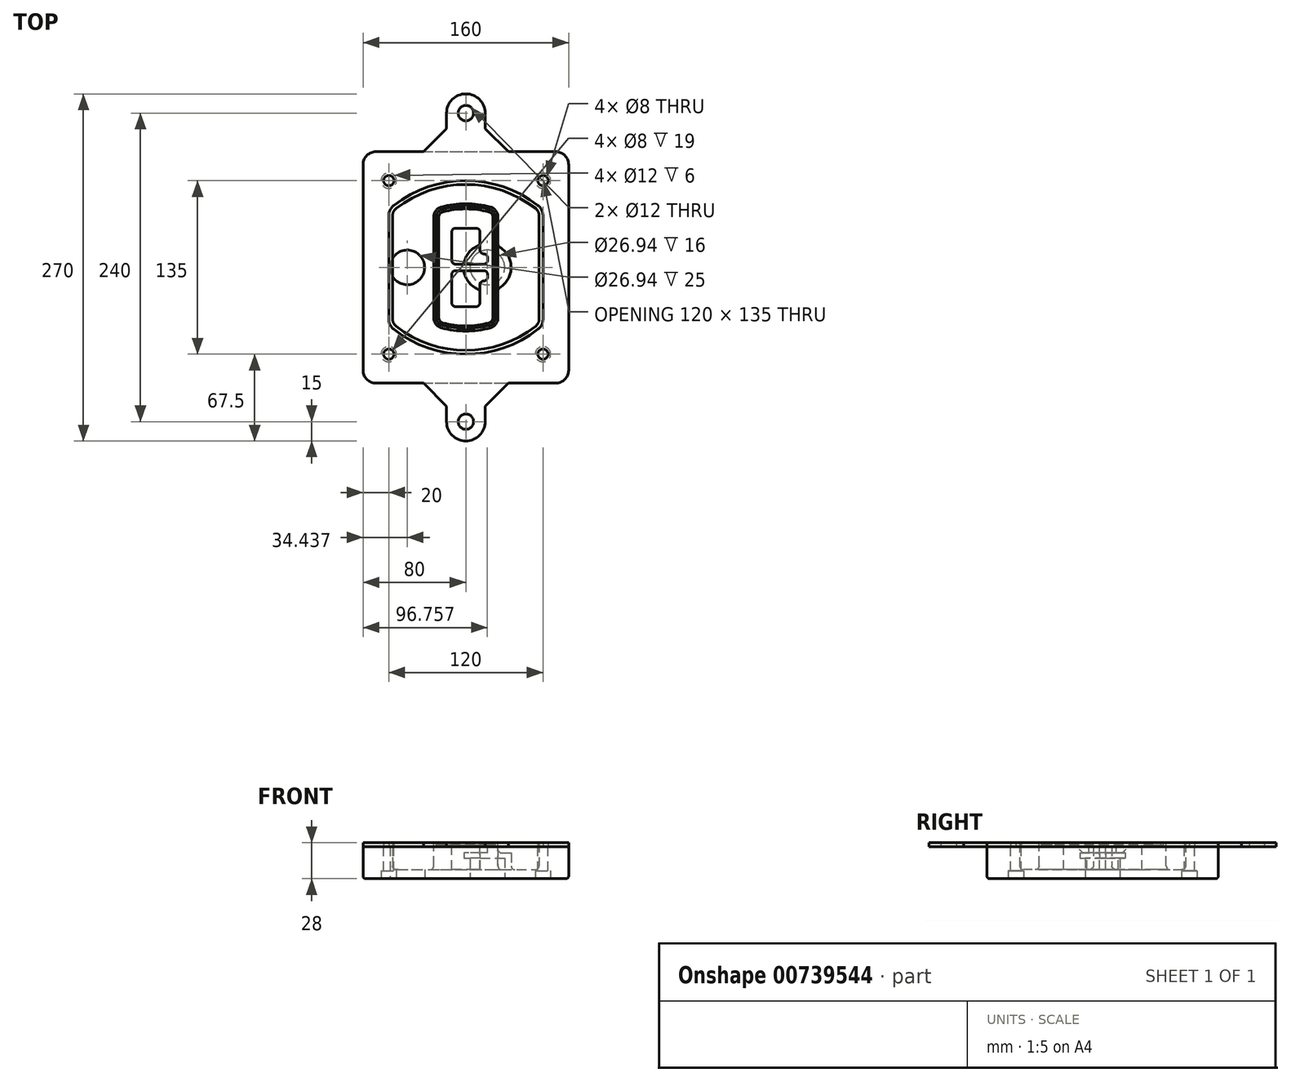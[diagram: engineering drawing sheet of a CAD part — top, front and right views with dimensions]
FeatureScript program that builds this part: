
annotation { "Feature Type Name" : "Feature", "Feature Type Description" : "" }
export const myFeature = defineFeature(function(context is Context, id is Id, definition is map)
    precondition{}
    {
        {
            var Q0;
            Q0=qCreatedBy(makeId("Top.planeOp"),FACE);
            var sketch = newSketch(context, id + "F0", { "sketchPlane" : qUnion([Q0])});
            skPoint(sketch, "E0.rect.middle", {"position": v(0, 0) * mm});
            skLineSegment(sketch, "E1.bottom", {"start": v(-70, -90) * mm, "end": v(70, -90) * mm});
            skLineSegment(sketch, "E1.top", {"start": v(-70, 90) * mm, "end": v(70, 90) * mm});
            skLineSegment(sketch, "E1.left", {"start": v(-80, -80) * mm, "end": v(-80, 80) * mm});
            skLineSegment(sketch, "E1.right", {"start": v(80, -80) * mm, "end": v(80, 80) * mm});
            skLineSegment(sketch, "E2", {"start": v(-80, 90) * mm, "end": v(80, -90) * mm, "construction": true});
            skLineSegment(sketch, "E3", {"start": v(80, 90) * mm, "end": v(-80, -90) * mm, "construction": true});
            skCircle(sketch, "E4", {"center": v(-60, 67.5) * mm, "radius": 4 * mm});
            skCircle(sketch, "E5", {"center": v(60, 67.5) * mm, "radius": 4 * mm});
            skCircle(sketch, "E6", {"center": v(60, -67.5) * mm, "radius": 4 * mm});
            skCircle(sketch, "E7", {"center": v(-60, -67.5) * mm, "radius": 4 * mm});
            skLineSegment(sketch, "E8", {"start": v(-60, 67.5) * mm, "end": v(60, 67.5) * mm, "construction": true});
            skLineSegment(sketch, "E9", {"start": v(60, 67.5) * mm, "end": v(60, -67.5) * mm, "construction": true});
            skLineSegment(sketch, "E10", {"start": v(60, -67.5) * mm, "end": v(-60, -67.5) * mm, "construction": true});
            skLineSegment(sketch, "E11", {"start": v(-60, -67.5) * mm, "end": v(-60, 67.5) * mm, "construction": true});
            skLineSegment(sketch, "E12", {"start": v(-60, 40.3) * mm, "end": v(-60, -40.3) * mm});
            skLineSegment(sketch, "E13", {"start": v(60, 40.3) * mm, "end": v(60, -40.3) * mm});
            skArc(sketch, "E14", {"start": v(56.15, 48.18) * mm, "mid": v(0, 67.5) * mm, "end": v(-56.15, 48.18) * mm});
            skArc(sketch, "E15", {"start": v(-56.15, -48.18) * mm, "mid": v(0, -67.5) * mm, "end": v(56.15, -48.18) * mm});
            skLineSegment(sketch, "E16", {"start": v(-60, 0) * mm, "end": v(60, 0) * mm, "construction": true});
            skPoint(sketch, "E17.visualSharp", {"position": v(-60, -45) * mm});
            skArc(sketch, "E17.filletArc", {"start": v(-60, -40.3) * mm, "mid": v(-58.99, -44.68) * mm, "end": v(-56.15, -48.18) * mm});
            skPoint(sketch, "E18.visualSharp", {"position": v(-60, 45) * mm});
            skArc(sketch, "E18.filletArc", {"start": v(-56.15, 48.18) * mm, "mid": v(-58.99, 44.68) * mm, "end": v(-60, 40.3) * mm});
            skPoint(sketch, "E19.visualSharp", {"position": v(60, 45) * mm});
            skArc(sketch, "E19.filletArc", {"start": v(60, 40.3) * mm, "mid": v(58.99, 44.68) * mm, "end": v(56.15, 48.18) * mm});
            skPoint(sketch, "E20.visualSharp", {"position": v(60, -45) * mm});
            skArc(sketch, "E20.filletArc", {"start": v(56.15, -48.18) * mm, "mid": v(58.99, -44.68) * mm, "end": v(60, -40.3) * mm});
            skPoint(sketch, "E21.visualSharp", {"position": v(-80, 90) * mm});
            skArc(sketch, "E21.filletArc", {"start": v(-70, 90) * mm, "mid": v(-77.07, 87.07) * mm, "end": v(-80, 80) * mm});
            skPoint(sketch, "E22.visualSharp", {"position": v(80, 90) * mm});
            skArc(sketch, "E22.filletArc", {"start": v(80, 80) * mm, "mid": v(77.07, 87.07) * mm, "end": v(70, 90) * mm});
            skPoint(sketch, "E23.visualSharp", {"position": v(80, -90) * mm});
            skArc(sketch, "E23.filletArc", {"start": v(70, -90) * mm, "mid": v(77.07, -87.07) * mm, "end": v(80, -80) * mm});
            skPoint(sketch, "E24.visualSharp", {"position": v(-80, -90) * mm});
            skArc(sketch, "E24.filletArc", {"start": v(-80, -80) * mm, "mid": v(-77.07, -87.07) * mm, "end": v(-70, -90) * mm});
            skArc(sketch, "E25.0", {"start": v(57, 40.3) * mm, "mid": v(56.3, 43.36) * mm, "end": v(54.3, 45.81) * mm});
            skLineSegment(sketch, "E25.1", {"start": v(57, 40.3) * mm, "end": v(57, -40.3) * mm});
            skArc(sketch, "E25.2", {"start": v(54.3, -45.81) * mm, "mid": v(56.3, -43.36) * mm, "end": v(57, -40.3) * mm});
            skArc(sketch, "E25.3", {"start": v(-54.3, -45.81) * mm, "mid": v(0, -64.5) * mm, "end": v(54.3, -45.81) * mm});
            skArc(sketch, "E25.4", {"start": v(-57, -40.3) * mm, "mid": v(-56.3, -43.36) * mm, "end": v(-54.3, -45.81) * mm});
            skArc(sketch, "E25.5", {"start": v(54.3, 45.81) * mm, "mid": v(0, 64.5) * mm, "end": v(-54.3, 45.81) * mm});
            skLineSegment(sketch, "E25.6", {"start": v(-57, 40.3) * mm, "end": v(-57, -40.3) * mm});
            skArc(sketch, "E25.7", {"start": v(-54.3, 45.81) * mm, "mid": v(-56.3, 43.36) * mm, "end": v(-57, 40.3) * mm});
            skArc(sketch, "E26.0", {"start": v(-58.62, 51.33) * mm, "mid": v(-62.58, 46.43) * mm, "end": v(-64, 40.3) * mm});
            skArc(sketch, "E26.1", {"start": v(58.62, 51.33) * mm, "mid": v(0, 71.5) * mm, "end": v(-58.62, 51.33) * mm});
            skArc(sketch, "E26.2", {"start": v(64, 40.3) * mm, "mid": v(62.58, 46.43) * mm, "end": v(58.62, 51.33) * mm});
            skLineSegment(sketch, "E26.3", {"start": v(64, 40.3) * mm, "end": v(64, -40.3) * mm});
            skArc(sketch, "E26.4", {"start": v(58.62, -51.33) * mm, "mid": v(62.58, -46.43) * mm, "end": v(64, -40.3) * mm});
            skLineSegment(sketch, "E26.5", {"start": v(-64, 40.3) * mm, "end": v(-64, -40.3) * mm});
            skArc(sketch, "E26.6", {"start": v(-58.62, -51.33) * mm, "mid": v(0, -71.5) * mm, "end": v(58.62, -51.33) * mm});
            skArc(sketch, "E26.7", {"start": v(-64, -40.3) * mm, "mid": v(-62.58, -46.43) * mm, "end": v(-58.62, -51.33) * mm});
            skSolve(sketch);
        }
        {
            var Q0;
            Q0=makeQuery(id+"F0.imprint","IMPRINT",FACE,{"disambiguationData":[TD([[makeQuery(id+"F0.imprint","IMPRINT",EDGE,{"derivedFrom":sQuery(id+"F0.wireOp",EDGE,"E1.bottom")}),1.0]])]});
            var Q1;
            Q1=makeQuery(id+"F0.imprint","IMPRINT",FACE,{"disambiguationData":[TD([[makeQuery(id+"F0.imprint","IMPRINT",EDGE,{"derivedFrom":sQuery(id+"F0.wireOp",EDGE,"E12")}),1.0]])]});
            var Q2;
            Q2=makeQuery(id+"F0.imprint","IMPRINT",FACE,{"disambiguationData":[TD([[makeQuery(id+"F0.imprint","IMPRINT",EDGE,{"derivedFrom":sQuery(id+"F0.wireOp",EDGE,"E25.0")}),1.0]])]});
            var Q3;
            Q3=makeQuery(id+"F0.imprint","IMPRINT",FACE,{"disambiguationData":[TD([[makeQuery(id+"F0.imprint","IMPRINT",EDGE,{"derivedFrom":sQuery(id+"F0.wireOp",EDGE,"E12")}),-1.0]])]});
            extrude(context, id + "F1", {"entities" : qUnion([Q0, Q1, Q2, Q3]), "oppositeDirection" : true, "depth" : 25 * mm});
        }
        {
            var Q0;
            Q0=makeQuery(id+"F0.imprint","IMPRINT",FACE,{"disambiguationData":[TD([[makeQuery(id+"F0.imprint","IMPRINT",EDGE,{"derivedFrom":sQuery(id+"F0.wireOp",EDGE,"E12")}),1.0]])]});
            extrude(context, id + "F2", {"entities" : qUnion([Q0]), "operationType" : NewBodyOperationType.ADD, "depth" : 3 * mm, "offsetDistance" : 25 * mm});
        }
        {
            var Q0;
            Q0=makeQuery(id+"F0.imprint","IMPRINT",FACE,{"disambiguationData":[TD([[makeQuery(id+"F0.imprint","IMPRINT",EDGE,{"derivedFrom":sQuery(id+"F0.wireOp",EDGE,"E25.0")}),1.0]])]});
            extrude(context, id + "F3", {"entities" : qUnion([Q0]), "operationType" : NewBodyOperationType.REMOVE, "oppositeDirection" : true, "depth" : 18 * mm});
        }
        {
            var Q0;
            Q0=makeQuery(id+"F2.opExtrude","CAP_FACE",FACE,{"disambiguationData":[OSD([sQuery(id+"F0.wireOp",EDGE,"E12"),sQuery(id+"F0.wireOp",EDGE,"E13"),sQuery(id+"F0.wireOp",EDGE,"E14"),sQuery(id+"F0.wireOp",EDGE,"E15"),sQuery(id+"F0.wireOp",EDGE,"E17.filletArc"),sQuery(id+"F0.wireOp",EDGE,"E18.filletArc"),sQuery(id+"F0.wireOp",EDGE,"E19.filletArc"),sQuery(id+"F0.wireOp",EDGE,"E20.filletArc"),sQuery(id+"F0.wireOp",EDGE,"E25.0"),sQuery(id+"F0.wireOp",EDGE,"E25.1"),sQuery(id+"F0.wireOp",EDGE,"E25.2"),sQuery(id+"F0.wireOp",EDGE,"E25.3"),sQuery(id+"F0.wireOp",EDGE,"E25.4"),sQuery(id+"F0.wireOp",EDGE,"E25.5"),sQuery(id+"F0.wireOp",EDGE,"E25.6"),sQuery(id+"F0.wireOp",EDGE,"E25.7")])],"isStart":false});
            var sketch = newSketch(context, id + "F4", { "sketchPlane" : qUnion([Q0])});
            skArc(sketch, "E27.0", {"start": v(-19.08, -46.97) * mm, "mid": v(0, -49.5) * mm, "end": v(19.08, -46.97) * mm});
            skArc(sketch, "E28.0", {"start": v(19.08, 46.97) * mm, "mid": v(0, 49.5) * mm, "end": v(-19.08, 46.97) * mm});
            skLineSegment(sketch, "E29", {"start": v(-25, 39.25) * mm, "end": v(-25, -39.25) * mm});
            skLineSegment(sketch, "E30", {"start": v(25, 39.25) * mm, "end": v(25, -39.25) * mm});
            skLineSegment(sketch, "E31", {"start": v(-25, 45.1) * mm, "end": v(25, 45.1) * mm, "construction": true});
            skLineSegment(sketch, "E32", {"start": v(-25, -45.1) * mm, "end": v(25, -45.1) * mm, "construction": true});
            skPoint(sketch, "E33.visualSharp", {"position": v(-25, 45.1) * mm});
            skArc(sketch, "E33.filletArc", {"start": v(-19.08, 46.97) * mm, "mid": v(-23.35, 44.11) * mm, "end": v(-25, 39.25) * mm});
            skPoint(sketch, "E34.visualSharp", {"position": v(25, 45.1) * mm});
            skArc(sketch, "E34.filletArc", {"start": v(25, 39.25) * mm, "mid": v(23.35, 44.11) * mm, "end": v(19.08, 46.97) * mm});
            skPoint(sketch, "E35.visualSharp", {"position": v(25, -45.1) * mm});
            skArc(sketch, "E35.filletArc", {"start": v(19.08, -46.97) * mm, "mid": v(23.35, -44.11) * mm, "end": v(25, -39.25) * mm});
            skPoint(sketch, "E36.visualSharp", {"position": v(-25, -45.1) * mm});
            skArc(sketch, "E36.filletArc", {"start": v(-25, -39.25) * mm, "mid": v(-23.35, -44.11) * mm, "end": v(-19.08, -46.97) * mm});
            skArc(sketch, "E37.0", {"start": v(54.3, 45.81) * mm, "mid": v(0, 64.5) * mm, "end": v(-54.3, 45.81) * mm});
            skArc(sketch, "E37.1", {"start": v(-54.3, 45.81) * mm, "mid": v(-56.3, 43.36) * mm, "end": v(-57, 40.3) * mm});
            skLineSegment(sketch, "E37.2", {"start": v(-57, 40.3) * mm, "end": v(-57, -40.3) * mm});
            skArc(sketch, "E37.3", {"start": v(-57, -40.3) * mm, "mid": v(-56.3, -43.36) * mm, "end": v(-54.3, -45.81) * mm});
            skArc(sketch, "E37.4", {"start": v(-54.3, -45.81) * mm, "mid": v(0, -64.5) * mm, "end": v(54.3, -45.81) * mm});
            skArc(sketch, "E37.5", {"start": v(54.3, -45.81) * mm, "mid": v(56.3, -43.36) * mm, "end": v(57, -40.3) * mm});
            skLineSegment(sketch, "E37.6", {"start": v(57, 40.3) * mm, "end": v(57, -40.3) * mm});
            skArc(sketch, "E37.7", {"start": v(57, 40.3) * mm, "mid": v(56.3, 43.36) * mm, "end": v(54.3, 45.81) * mm});
            skLineSegment(sketch, "E38.0", {"start": v(23, 39.25) * mm, "end": v(23, -39.25) * mm});
            skArc(sketch, "E38.1", {"start": v(18.56, -45.04) * mm, "mid": v(21.76, -42.9) * mm, "end": v(23, -39.25) * mm});
            skArc(sketch, "E38.2", {"start": v(-18.56, -45.04) * mm, "mid": v(0, -47.5) * mm, "end": v(18.56, -45.04) * mm});
            skArc(sketch, "E38.3", {"start": v(-23, -39.25) * mm, "mid": v(-21.76, -42.9) * mm, "end": v(-18.56, -45.04) * mm});
            skLineSegment(sketch, "E38.4", {"start": v(-23, 39.25) * mm, "end": v(-23, -39.25) * mm});
            skArc(sketch, "E38.5", {"start": v(23, 39.25) * mm, "mid": v(21.76, 42.9) * mm, "end": v(18.56, 45.04) * mm});
            skArc(sketch, "E38.6", {"start": v(-18.56, 45.04) * mm, "mid": v(-21.76, 42.9) * mm, "end": v(-23, 39.25) * mm});
            skArc(sketch, "E38.7", {"start": v(18.56, 45.04) * mm, "mid": v(0, 47.5) * mm, "end": v(-18.56, 45.04) * mm});
            skArc(sketch, "E39.0", {"start": v(21, 39.25) * mm, "mid": v(20.18, 41.68) * mm, "end": v(18.04, 43.1) * mm});
            skLineSegment(sketch, "E39.1", {"start": v(21, 39.25) * mm, "end": v(21, -39.25) * mm});
            skArc(sketch, "E39.2", {"start": v(18.04, -43.1) * mm, "mid": v(20.18, -41.68) * mm, "end": v(21, -39.25) * mm});
            skArc(sketch, "E39.3", {"start": v(-18.04, -43.1) * mm, "mid": v(0, -45.5) * mm, "end": v(18.04, -43.1) * mm});
            skArc(sketch, "E39.4", {"start": v(-21, -39.25) * mm, "mid": v(-20.18, -41.68) * mm, "end": v(-18.04, -43.1) * mm});
            skArc(sketch, "E39.5", {"start": v(18.04, 43.1) * mm, "mid": v(0, 45.5) * mm, "end": v(-18.04, 43.1) * mm});
            skLineSegment(sketch, "E39.6", {"start": v(-21, 39.25) * mm, "end": v(-21, -39.25) * mm});
            skArc(sketch, "E39.7", {"start": v(-18.04, 43.1) * mm, "mid": v(-20.18, 41.68) * mm, "end": v(-21, 39.25) * mm});
            skLineSegment(sketch, "E40", {"start": v(-25, 0) * mm, "end": v(25, 0) * mm, "construction": true});
            skLineSegment(sketch, "E41", {"start": v(-11, 5.5) * mm, "end": v(-11, 27.5) * mm});
            skLineSegment(sketch, "E42", {"start": v(-8, 30.5) * mm, "end": v(8, 30.5) * mm});
            skLineSegment(sketch, "E43", {"start": v(11, 27.5) * mm, "end": v(11, 13.5) * mm});
            skLineSegment(sketch, "E44", {"start": v(14, 10.5) * mm, "end": v(14, 10.5) * mm});
            skLineSegment(sketch, "E45", {"start": v(17, 7.5) * mm, "end": v(17, 5.5) * mm});
            skLineSegment(sketch, "E46", {"start": v(14, 2.5) * mm, "end": v(-8, 2.5) * mm});
            skPoint(sketch, "E47.visualSharp", {"position": v(-11, 30.5) * mm});
            skArc(sketch, "E47.filletArc", {"start": v(-8, 30.5) * mm, "mid": v(-10.12, 29.62) * mm, "end": v(-11, 27.5) * mm});
            skPoint(sketch, "E48.visualSharp", {"position": v(11, 30.5) * mm});
            skArc(sketch, "E48.filletArc", {"start": v(11, 27.5) * mm, "mid": v(10.12, 29.62) * mm, "end": v(8, 30.5) * mm});
            skPoint(sketch, "E49.visualSharp", {"position": v(11, 10.5) * mm});
            skArc(sketch, "E49.filletArc", {"start": v(11, 13.5) * mm, "mid": v(11.88, 11.38) * mm, "end": v(14, 10.5) * mm});
            skPoint(sketch, "E50.visualSharp", {"position": v(17, 10.5) * mm});
            skArc(sketch, "E50.filletArc", {"start": v(17, 7.5) * mm, "mid": v(16.12, 9.62) * mm, "end": v(14, 10.5) * mm});
            skPoint(sketch, "E51.visualSharp", {"position": v(17, 2.5) * mm});
            skArc(sketch, "E51.filletArc", {"start": v(14, 2.5) * mm, "mid": v(16.12, 3.38) * mm, "end": v(17, 5.5) * mm});
            skPoint(sketch, "E52.visualSharp", {"position": v(-11, 2.5) * mm});
            skArc(sketch, "E52.filletArc", {"start": v(-11, 5.5) * mm, "mid": v(-10.12, 3.38) * mm, "end": v(-8, 2.5) * mm});
            skLineSegment(sketch, "E53.0.MirrorCS", {"start": v(14, -2.5) * mm, "end": v(-8, -2.5) * mm});
            skArc(sketch, "E54.0.MirrorCS", {"start": v(-11, -5.5) * mm, "mid": v(-10.12, -3.38) * mm, "end": v(-8, -2.5) * mm});
            skLineSegment(sketch, "E55.0.MirrorCS", {"start": v(-11, -5.5) * mm, "end": v(-11, -27.5) * mm});
            skArc(sketch, "E56.0.MirrorCS", {"start": v(-8, -30.5) * mm, "mid": v(-10.12, -29.62) * mm, "end": v(-11, -27.5) * mm});
            skLineSegment(sketch, "E57.0.MirrorCS", {"start": v(-8, -30.5) * mm, "end": v(8, -30.5) * mm});
            skArc(sketch, "E58.0.MirrorCS", {"start": v(11, -27.5) * mm, "mid": v(10.12, -29.62) * mm, "end": v(8, -30.5) * mm});
            skLineSegment(sketch, "E59.0.MirrorCS", {"start": v(11, -27.5) * mm, "end": v(11, -13.5) * mm});
            skArc(sketch, "E60.0.MirrorCS", {"start": v(11, -13.5) * mm, "mid": v(11.88, -11.38) * mm, "end": v(14, -10.5) * mm});
            skArc(sketch, "E61.0.MirrorCS", {"start": v(17, -7.5) * mm, "mid": v(16.12, -9.62) * mm, "end": v(14, -10.5) * mm});
            skLineSegment(sketch, "E62.0.MirrorCS", {"start": v(17, -7.5) * mm, "end": v(17, -5.5) * mm});
            skArc(sketch, "E63.0.MirrorCS", {"start": v(14, -2.5) * mm, "mid": v(16.12, -3.38) * mm, "end": v(17, -5.5) * mm});
            skSolve(sketch);
        }
        {
            var Q0;
            Q0=makeQuery(id+"F4.imprint","IMPRINT",FACE,{"disambiguationData":[TD([[makeQuery(id+"F4.imprint","IMPRINT",EDGE,{"derivedFrom":sQuery(id+"F4.wireOp",EDGE,"E27.0")}),1.0]])]});
            var Q1;
            Q1=makeQuery(id+"F4.imprint","IMPRINT",FACE,{"disambiguationData":[TD([[makeQuery(id+"F4.imprint","IMPRINT",EDGE,{"derivedFrom":sQuery(id+"F4.wireOp",EDGE,"E38.0")}),-1.0]])]});
            var Q2;
            Q2=makeQuery(id+"F4.imprint","IMPRINT",FACE,{"disambiguationData":[TD([[makeQuery(id+"F4.imprint","IMPRINT",EDGE,{"derivedFrom":sQuery(id+"F4.wireOp",EDGE,"E39.0")}),1.0]])]});
            extrude(context, id + "F5", {"entities" : qUnion([Q0, Q1, Q2]), "operationType" : NewBodyOperationType.ADD, "endBound" : BoundingType.UP_TO_NEXT, "oppositeDirection" : true, "depth" : 25 * mm});
        }
        {
            var Q0;
            Q0=makeQuery(id+"F4.imprint","IMPRINT",FACE,{"disambiguationData":[TD([[makeQuery(id+"F4.imprint","IMPRINT",EDGE,{"derivedFrom":sQuery(id+"F4.wireOp",EDGE,"E38.0")}),-1.0]])]});
            extrude(context, id + "F6", {"entities" : qUnion([Q0]), "operationType" : NewBodyOperationType.REMOVE, "oppositeDirection" : true, "depth" : 2 * mm});
        }
        {
            var Q0;
            Q0=makeQuery(id+"F1.opExtrude","CAP_FACE",FACE,{"disambiguationData":[OSD([sQuery(id+"F0.wireOp",EDGE,"E1.bottom"),sQuery(id+"F0.wireOp",EDGE,"E1.top"),sQuery(id+"F0.wireOp",EDGE,"E1.left"),sQuery(id+"F0.wireOp",EDGE,"E1.right"),sQuery(id+"F0.wireOp",EDGE,"E4"),sQuery(id+"F0.wireOp",EDGE,"E5"),sQuery(id+"F0.wireOp",EDGE,"E6"),sQuery(id+"F0.wireOp",EDGE,"E7"),sQuery(id+"F0.wireOp",EDGE,"E21.filletArc"),sQuery(id+"F0.wireOp",EDGE,"E22.filletArc"),sQuery(id+"F0.wireOp",EDGE,"E23.filletArc"),sQuery(id+"F0.wireOp",EDGE,"E24.filletArc")])],"isStart":false});
            var sketch = newSketch(context, id + "F7", { "sketchPlane" : qUnion([Q0])});
            skCircle(sketch, "E64", {"center": v(16.76, 0) * mm, "radius": 13.47 * mm});
            skCircle(sketch, "E65", {"center": v(-45.56, 0) * mm, "radius": 13.47 * mm});
            skLineSegment(sketch, "E66", {"start": v(80, 0) * mm, "end": v(-80, 0) * mm});
            skCircle(sketch, "E67", {"center": v(16.76, 0) * mm, "radius": 18.47 * mm});
            skCircle(sketch, "E68", {"center": v(60, -67.5) * mm, "radius": 6 * mm});
            skCircle(sketch, "E69", {"center": v(-60, -67.5) * mm, "radius": 6 * mm});
            skCircle(sketch, "E70", {"center": v(-60, 67.5) * mm, "radius": 6 * mm});
            skCircle(sketch, "E71", {"center": v(60, 67.5) * mm, "radius": 6 * mm});
            skSolve(sketch);
        }
        {
            var Q0;
            {var subQ1=sQuery(id+"F7.wireOp",EDGE,"E66");var subQ4=sQuery(id+"F7.wireOp",EDGE,"E64");var subQ6=makeQuery(id+"F7.imprint","INTERSECT",VERTEX,{"disambiguationData":[OD(0.0)],"derivedFrom":[subQ4,subQ1]});Q0=makeQuery(id+"F7.imprint","IMPRINT",FACE,{"disambiguationData":[TD([[makeQuery(id+"F7.imprint","IMPRINT",EDGE,{"disambiguationData":[TD([[subQ6,-1.0]])],"derivedFrom":subQ4}),-1.0]])]});}
            var Q1;
            {var subQ0=sQuery(id+"F7.wireOp",EDGE,"E66");var subQ1=sQuery(id+"F7.wireOp",EDGE,"E64");var subQ3=makeQuery(id+"F7.imprint","INTERSECT",VERTEX,{"disambiguationData":[OD(0.0)],"derivedFrom":[subQ1,subQ0]});Q1=makeQuery(id+"F7.imprint","IMPRINT",FACE,{"disambiguationData":[TD([[makeQuery(id+"F7.imprint","IMPRINT",EDGE,{"disambiguationData":[TD([[subQ3,-1.0]])],"derivedFrom":subQ1}),1.0]])]});}
            var Q2;
            {var subQ0=sQuery(id+"F7.wireOp",EDGE,"E66");var subQ1=sQuery(id+"F7.wireOp",EDGE,"E64");var subQ3=makeQuery(id+"F7.imprint","INTERSECT",VERTEX,{"disambiguationData":[OD(0.0)],"derivedFrom":[subQ1,subQ0]});Q2=makeQuery(id+"F7.imprint","IMPRINT",FACE,{"disambiguationData":[TD([[makeQuery(id+"F7.imprint","IMPRINT",EDGE,{"disambiguationData":[TD([[subQ3,1.0]])],"derivedFrom":subQ1}),1.0]])]});}
            var Q3;
            {var subQ1=sQuery(id+"F7.wireOp",EDGE,"E66");var subQ4=sQuery(id+"F7.wireOp",EDGE,"E64");var subQ6=makeQuery(id+"F7.imprint","INTERSECT",VERTEX,{"disambiguationData":[OD(0.0)],"derivedFrom":[subQ4,subQ1]});Q3=makeQuery(id+"F7.imprint","IMPRINT",FACE,{"disambiguationData":[TD([[makeQuery(id+"F7.imprint","IMPRINT",EDGE,{"disambiguationData":[TD([[subQ6,1.0]])],"derivedFrom":subQ4}),-1.0]])]});}
            extrude(context, id + "F8", {"entities" : qUnion([Q0, Q1, Q2, Q3]), "operationType" : NewBodyOperationType.ADD, "oppositeDirection" : true, "depth" : 20 * mm});
        }
        {
            var Q0;
            {var subQ0=sQuery(id+"F7.wireOp",EDGE,"E66");var subQ1=sQuery(id+"F7.wireOp",EDGE,"E64");var subQ3=makeQuery(id+"F7.imprint","INTERSECT",VERTEX,{"disambiguationData":[OD(0.0)],"derivedFrom":[subQ1,subQ0]});Q0=makeQuery(id+"F7.imprint","IMPRINT",FACE,{"disambiguationData":[TD([[makeQuery(id+"F7.imprint","IMPRINT",EDGE,{"disambiguationData":[TD([[subQ3,-1.0]])],"derivedFrom":subQ1}),1.0]])]});}
            var Q1;
            {var subQ0=sQuery(id+"F7.wireOp",EDGE,"E66");var subQ1=sQuery(id+"F7.wireOp",EDGE,"E64");var subQ3=makeQuery(id+"F7.imprint","INTERSECT",VERTEX,{"disambiguationData":[OD(0.0)],"derivedFrom":[subQ1,subQ0]});Q1=makeQuery(id+"F7.imprint","IMPRINT",FACE,{"disambiguationData":[TD([[makeQuery(id+"F7.imprint","IMPRINT",EDGE,{"disambiguationData":[TD([[subQ3,1.0]])],"derivedFrom":subQ1}),1.0]])]});}
            extrude(context, id + "F9", {"entities" : qUnion([Q0, Q1]), "operationType" : NewBodyOperationType.REMOVE, "oppositeDirection" : true, "depth" : 16 * mm});
        }
        {
            var Q0;
            {var subQ0=sQuery(id+"F7.wireOp",EDGE,"E66");var subQ1=sQuery(id+"F7.wireOp",EDGE,"E65");var subQ3=makeQuery(id+"F7.imprint","INTERSECT",VERTEX,{"disambiguationData":[OD(0.0)],"derivedFrom":[subQ1,subQ0]});Q0=makeQuery(id+"F7.imprint","IMPRINT",FACE,{"disambiguationData":[TD([[makeQuery(id+"F7.imprint","IMPRINT",EDGE,{"disambiguationData":[TD([[subQ3,-1.0]])],"derivedFrom":subQ1}),1.0]])]});}
            var Q1;
            {var subQ0=sQuery(id+"F7.wireOp",EDGE,"E66");var subQ1=sQuery(id+"F7.wireOp",EDGE,"E65");var subQ3=makeQuery(id+"F7.imprint","INTERSECT",VERTEX,{"disambiguationData":[OD(0.0)],"derivedFrom":[subQ1,subQ0]});Q1=makeQuery(id+"F7.imprint","IMPRINT",FACE,{"disambiguationData":[TD([[makeQuery(id+"F7.imprint","IMPRINT",EDGE,{"disambiguationData":[TD([[subQ3,1.0]])],"derivedFrom":subQ1}),1.0]])]});}
            extrude(context, id + "F10", {"entities" : qUnion([Q0, Q1]), "operationType" : NewBodyOperationType.REMOVE, "oppositeDirection" : true, "depth" : 25 * mm, "offsetDistance" : 25 * mm});
        }
        {
            var Q0;
            Q0=makeQuery(id+"F7.imprint","IMPRINT",FACE,{"disambiguationData":[TD([[makeQuery(id+"F7.imprint","IMPRINT",EDGE,{"derivedFrom":sQuery(id+"F7.wireOp",EDGE,"E68")}),1.0]])]});
            var Q1;
            Q1=makeQuery(id+"F7.imprint","IMPRINT",FACE,{"disambiguationData":[TD([[makeQuery(id+"F7.imprint","IMPRINT",EDGE,{"derivedFrom":makeQuery(id+"F1.opExtrude","CAP_EDGE",EDGE,{"disambiguationData":[OSD([sQuery(id+"F0.wireOp",EDGE,"E5")])],"isStart":false})}),-1.0]])]});
            var Q2;
            Q2=makeQuery(id+"F7.imprint","IMPRINT",FACE,{"disambiguationData":[TD([[makeQuery(id+"F7.imprint","IMPRINT",EDGE,{"derivedFrom":sQuery(id+"F7.wireOp",EDGE,"E69")}),1.0]])]});
            var Q3;
            Q3=makeQuery(id+"F7.imprint","IMPRINT",FACE,{"disambiguationData":[TD([[makeQuery(id+"F7.imprint","IMPRINT",EDGE,{"derivedFrom":makeQuery(id+"F1.opExtrude","CAP_EDGE",EDGE,{"disambiguationData":[OSD([sQuery(id+"F0.wireOp",EDGE,"E4")])],"isStart":false})}),-1.0]])]});
            var Q4;
            Q4=makeQuery(id+"F7.imprint","IMPRINT",FACE,{"disambiguationData":[TD([[makeQuery(id+"F7.imprint","IMPRINT",EDGE,{"derivedFrom":sQuery(id+"F7.wireOp",EDGE,"E70")}),1.0]])]});
            var Q5;
            Q5=makeQuery(id+"F7.imprint","IMPRINT",FACE,{"disambiguationData":[TD([[makeQuery(id+"F7.imprint","IMPRINT",EDGE,{"derivedFrom":makeQuery(id+"F1.opExtrude","CAP_EDGE",EDGE,{"disambiguationData":[OSD([sQuery(id+"F0.wireOp",EDGE,"E7")])],"isStart":false})}),-1.0]])]});
            var Q6;
            Q6=makeQuery(id+"F7.imprint","IMPRINT",FACE,{"disambiguationData":[TD([[makeQuery(id+"F7.imprint","IMPRINT",EDGE,{"derivedFrom":sQuery(id+"F7.wireOp",EDGE,"E71")}),1.0]])]});
            var Q7;
            Q7=makeQuery(id+"F7.imprint","IMPRINT",FACE,{"disambiguationData":[TD([[makeQuery(id+"F7.imprint","IMPRINT",EDGE,{"derivedFrom":makeQuery(id+"F1.opExtrude","CAP_EDGE",EDGE,{"disambiguationData":[OSD([sQuery(id+"F0.wireOp",EDGE,"E6")])],"isStart":false})}),-1.0]])]});
            extrude(context, id + "F11", {"entities" : qUnion([Q0, Q1, Q2, Q3, Q4, Q5, Q6, Q7]), "operationType" : NewBodyOperationType.REMOVE, "oppositeDirection" : true, "depth" : 6 * mm});
        }
        {
            var Q0;
            Q0=makeQuery(id+"F9.boolean.opBoolean","COPY",FACE,{"derivedFrom":makeQuery(id+"F9.opExtrude","CAP_FACE",FACE,{"disambiguationData":[OSD([sQuery(id+"F7.wireOp",EDGE,"E64")])],"isStart":false})});
            var sketch = newSketch(context, id + "F12", { "sketchPlane" : qUnion([Q0])});
            skArc(sketch, "E72.0", {"start": v(11, 17.55) * mm, "mid": v(2.57, 11.82) * mm, "end": v(-1.54, 2.5) * mm});
            skArc(sketch, "E72.1", {"start": v(-1.54, -2.5) * mm, "mid": v(2.57, -11.82) * mm, "end": v(11, -17.55) * mm});
            skLineSegment(sketch, "E73", {"start": v(-1.54, -2.5) * mm, "end": v(14, -2.5) * mm});
            skLineSegment(sketch, "E74.0", {"start": v(14, 2.5) * mm, "end": v(-1.54, 2.5) * mm});
            skArc(sketch, "E74.1", {"start": v(14, 2.5) * mm, "mid": v(16.12, 3.38) * mm, "end": v(17, 5.5) * mm});
            skLineSegment(sketch, "E74.2", {"start": v(17, 7.5) * mm, "end": v(17, 5.5) * mm});
            skArc(sketch, "E74.3", {"start": v(17, 7.5) * mm, "mid": v(16.12, 9.62) * mm, "end": v(14, 10.5) * mm});
            skArc(sketch, "E74.4", {"start": v(11, 13.5) * mm, "mid": v(11.88, 11.38) * mm, "end": v(14, 10.5) * mm});
            skLineSegment(sketch, "E74.5", {"start": v(11, 17.55) * mm, "end": v(11, 13.5) * mm});
            skLineSegment(sketch, "E74.7", {"start": v(14, -2.5) * mm, "end": v(-1.54, -2.5) * mm});
            skArc(sketch, "E74.8", {"start": v(14, -2.5) * mm, "mid": v(16.12, -3.38) * mm, "end": v(17, -5.5) * mm});
            skLineSegment(sketch, "E74.9", {"start": v(17, -7.5) * mm, "end": v(17, -5.5) * mm});
            skArc(sketch, "E74.10", {"start": v(17, -7.5) * mm, "mid": v(16.12, -9.62) * mm, "end": v(14, -10.5) * mm});
            skArc(sketch, "E74.11", {"start": v(11, -13.5) * mm, "mid": v(11.88, -11.38) * mm, "end": v(14, -10.5) * mm});
            skLineSegment(sketch, "E74.12", {"start": v(11, -17.55) * mm, "end": v(11, -13.5) * mm});
            skPoint(sketch, "E75.orphan", {"position": v(11, -27.5) * mm});
            skPoint(sketch, "E76.orphan", {"position": v(-8, -2.5) * mm});
            skPoint(sketch, "E77.orphan", {"position": v(-8, 2.5) * mm});
            skPoint(sketch, "E78.orphan", {"position": v(11, 27.5) * mm});
            skSolve(sketch);
        }
        {
            var Q0;
            {var subQ7=sQuery(id+"F12.wireOp",EDGE,"E72.0");var subQ14=sQuery(id+"F12.wireOp",EDGE,"E72.1");var subQ16=sQuery(id+"F12.wireOp",EDGE,"E74.1");var subQ18=sQuery(id+"F12.wireOp",EDGE,"E74.8");Q0=qUnion([makeQuery(id+"F12.imprint","IMPRINT",FACE,{"disambiguationData":[TD([[makeQuery(id+"F12.imprint","IMPRINT",EDGE,{"derivedFrom":subQ7}),1.0]])]}),makeQuery(id+"F12.imprint","IMPRINT",FACE,{"disambiguationData":[TD([[makeQuery(id+"F12.imprint","IMPRINT",EDGE,{"derivedFrom":subQ14}),1.0]])]}),makeQuery(id+"F12.imprint","IMPRINT",FACE,{"disambiguationData":[TD([[makeQuery(id+"F12.imprint","IMPRINT",EDGE,{"derivedFrom":subQ16}),1.0]])]}),makeQuery(id+"F12.imprint","IMPRINT",FACE,{"disambiguationData":[TD([[makeQuery(id+"F12.imprint","IMPRINT",EDGE,{"derivedFrom":subQ18}),-1.0]])]})]);}
            var Q1;
            Q1=makeQuery(id+"F5.boolean.opBoolean","SPLIT",FACE,{"disambiguationData":[TD([makeQuery(id+"F5.opExtrude","SWEPT_FACE",FACE,{"disambiguationData":[OSD([sQuery(id+"F4.wireOp",EDGE,"E41")])]})])],"derivedFrom":makeQuery(id+"F3.boolean.opBoolean","COPY",FACE,{"derivedFrom":makeQuery(id+"F3.opExtrude","CAP_FACE",FACE,{"disambiguationData":[OSD([sQuery(id+"F0.wireOp",EDGE,"E25.0"),sQuery(id+"F0.wireOp",EDGE,"E25.1"),sQuery(id+"F0.wireOp",EDGE,"E25.2"),sQuery(id+"F0.wireOp",EDGE,"E25.3"),sQuery(id+"F0.wireOp",EDGE,"E25.4"),sQuery(id+"F0.wireOp",EDGE,"E25.5"),sQuery(id+"F0.wireOp",EDGE,"E25.6"),sQuery(id+"F0.wireOp",EDGE,"E25.7")])],"isStart":false})})});
            extrude(context, id + "F13", {"entities" : qUnion([Q0]), "operationType" : NewBodyOperationType.REMOVE, "endBound" : BoundingType.UP_TO_SURFACE, "endBoundEntityFace" : qUnion([Q1]), "depth" : 25 * mm});
        }
        {
            var Q0;
            Q0=makeQuery(id+"F3.boolean.opBoolean","COPY",EDGE,{"derivedFrom":makeQuery(id+"F3.opExtrude","CAP_EDGE",EDGE,{"disambiguationData":[OSD([sQuery(id+"F0.wireOp",EDGE,"E25.6")])],"isStart":false})});
            var Q1;
            Q1=makeQuery(id+"F8.boolean.opBoolean","INTERSECT",EDGE,{"derivedFrom":[makeQuery(id+"F5.opExtrude","SWEPT_FACE",FACE,{"disambiguationData":[OSD([sQuery(id+"F4.wireOp",EDGE,"E30")])]}),makeQuery(id+"F8.opExtrude","CAP_FACE",FACE,{"disambiguationData":[OSD([sQuery(id+"F7.wireOp",EDGE,"E67")])],"isStart":false})]});
            var Q2;
            Q2=makeQuery(id+"F8.boolean.opBoolean","INTERSECT",EDGE,{"disambiguationData":[OD(1.0)],"derivedFrom":[makeQuery(id+"F5.opExtrude","SWEPT_FACE",FACE,{"disambiguationData":[OSD([sQuery(id+"F4.wireOp",EDGE,"E30")])]}),makeQuery(id+"F8.opExtrude","SWEPT_FACE",FACE,{"disambiguationData":[OSD([sQuery(id+"F7.wireOp",EDGE,"E67")])]})]});
            var Q3;
            {var subQ0=sQuery(id+"F4.wireOp",EDGE,"E30");Q3=makeQuery(id+"F8.boolean.opBoolean","SPLIT",EDGE,{"disambiguationData":[TD([makeQuery(id+"F5.opExtrude","SWEPT_FACE",FACE,{"disambiguationData":[OSD([sQuery(id+"F4.wireOp",EDGE,"E35.filletArc")])]})])],"derivedFrom":makeQuery(id+"F5.opExtrude","CAP_EDGE",EDGE,{"disambiguationData":[OSD([subQ0])],"isStart":false})});}
            var Q4;
            {var subQ0=sQuery(id+"F0.wireOp",EDGE,"E25.7");var subQ1=sQuery(id+"F0.wireOp",EDGE,"E25.1");var subQ2=sQuery(id+"F0.wireOp",EDGE,"E25.6");var subQ3=sQuery(id+"F0.wireOp",EDGE,"E25.5");var subQ4=sQuery(id+"F0.wireOp",EDGE,"E25.4");var subQ5=sQuery(id+"F0.wireOp",EDGE,"E25.0");var subQ6=sQuery(id+"F0.wireOp",EDGE,"E25.2");var subQ7=sQuery(id+"F0.wireOp",EDGE,"E25.3");Q4=makeQuery(id+"F8.boolean.opBoolean","INTERSECT",EDGE,{"derivedFrom":[makeQuery(id+"F5.boolean.opBoolean","SPLIT",FACE,{"disambiguationData":[TD([makeQuery(id+"F2.opExtrude","SWEPT_FACE",FACE,{"disambiguationData":[OSD([subQ5])]})])],"derivedFrom":makeQuery(id+"F3.boolean.opBoolean","COPY",FACE,{"derivedFrom":makeQuery(id+"F3.opExtrude","CAP_FACE",FACE,{"disambiguationData":[OSD([subQ5,subQ1,subQ6,subQ7,subQ4,subQ3,subQ2,subQ0])],"isStart":false})})}),makeQuery(id+"F8.opExtrude","SWEPT_FACE",FACE,{"disambiguationData":[OSD([sQuery(id+"F7.wireOp",EDGE,"E67")])]})]});}
            var Q5;
            Q5=makeQuery(id+"F8.boolean.opBoolean","INTERSECT",EDGE,{"disambiguationData":[OD(0.0)],"derivedFrom":[makeQuery(id+"F5.opExtrude","SWEPT_FACE",FACE,{"disambiguationData":[OSD([sQuery(id+"F4.wireOp",EDGE,"E30")])]}),makeQuery(id+"F8.opExtrude","SWEPT_FACE",FACE,{"disambiguationData":[OSD([sQuery(id+"F7.wireOp",EDGE,"E67")])]})]});
            fillet(context, id + "F14", {"entities" : qUnion([Q0, Q1, Q2, Q3, Q4, Q5]), "radius" : 3 * mm, "tangentPropagation" : true, "allowEdgeOverflow" : false});
        }
        {
            var Q0;
            Q0=makeQuery(id+"F1.opExtrude","CAP_EDGE",EDGE,{"disambiguationData":[OSD([sQuery(id+"F0.wireOp",EDGE,"E1.bottom")])],"isStart":false});
            fillet(context, id + "F15", {"entities" : qUnion([Q0]), "radius" : 2 * mm, "tangentPropagation" : true, "allowEdgeOverflow" : false});
        }
        {
            var Q0;
            {var subQ0=sQuery(id+"F0.wireOp",EDGE,"E21.filletArc");var subQ1=sQuery(id+"F0.wireOp",EDGE,"E7");var subQ2=sQuery(id+"F0.wireOp",EDGE,"E6");var subQ3=sQuery(id+"F0.wireOp",EDGE,"E5");var subQ4=sQuery(id+"F0.wireOp",EDGE,"E4");var subQ5=sQuery(id+"F0.wireOp",EDGE,"E22.filletArc");var subQ6=sQuery(id+"F0.wireOp",EDGE,"E1.bottom");var subQ7=sQuery(id+"F0.wireOp",EDGE,"E1.right");var subQ8=sQuery(id+"F0.wireOp",EDGE,"E1.top");var subQ9=sQuery(id+"F0.wireOp",EDGE,"E1.left");var subQ10=sQuery(id+"F0.wireOp",EDGE,"E23.filletArc");var subQ11=sQuery(id+"F0.wireOp",EDGE,"E24.filletArc");Q0=makeQuery(id+"F2.boolean.opBoolean","SPLIT",FACE,{"disambiguationData":[TD([makeQuery(id+"F1.opExtrude","SWEPT_FACE",FACE,{"disambiguationData":[OSD([subQ6])]})])],"derivedFrom":makeQuery(id+"F1.opExtrude","CAP_FACE",FACE,{"disambiguationData":[OSD([subQ6,subQ8,subQ9,subQ7,subQ4,subQ3,subQ2,subQ1,subQ0,subQ5,subQ10,subQ11])],"isStart":true})});}
            var sketch = newSketch(context, id + "F16", { "sketchPlane" : qUnion([Q0])});
            skLineSegment(sketch, "E79.0", {"start": v(-70, 90) * mm, "end": v(70, 90) * mm});
            skArc(sketch, "E79.1", {"start": v(-70, 90) * mm, "mid": v(-77.07, 87.07) * mm, "end": v(-80, 80) * mm});
            skLineSegment(sketch, "E79.2", {"start": v(-80, -80) * mm, "end": v(-80, 80) * mm});
            skArc(sketch, "E79.3", {"start": v(-80, -80) * mm, "mid": v(-77.07, -87.07) * mm, "end": v(-70, -90) * mm});
            skLineSegment(sketch, "E79.4", {"start": v(-70, -90) * mm, "end": v(70, -90) * mm});
            skArc(sketch, "E79.5", {"start": v(70, -90) * mm, "mid": v(77.07, -87.07) * mm, "end": v(80, -80) * mm});
            skLineSegment(sketch, "E79.6", {"start": v(80, -80) * mm, "end": v(80, 80) * mm});
            skArc(sketch, "E79.7", {"start": v(80, 80) * mm, "mid": v(77.07, 87.07) * mm, "end": v(70, 90) * mm});
            skCircle(sketch, "E79.8", {"center": v(60, 67.5) * mm, "radius": 4 * mm});
            skCircle(sketch, "E79.9", {"center": v(-60, 67.5) * mm, "radius": 4 * mm});
            skCircle(sketch, "E79.10", {"center": v(-60, -67.5) * mm, "radius": 4 * mm});
            skCircle(sketch, "E79.11", {"center": v(60, -67.5) * mm, "radius": 4 * mm});
            skArc(sketch, "E79.12", {"start": v(56.15, -48.18) * mm, "mid": v(58.99, -44.68) * mm, "end": v(60, -40.3) * mm});
            skArc(sketch, "E79.13", {"start": v(-56.15, -48.18) * mm, "mid": v(0, -67.5) * mm, "end": v(56.15, -48.18) * mm});
            skArc(sketch, "E79.14", {"start": v(-60, -40.3) * mm, "mid": v(-58.99, -44.68) * mm, "end": v(-56.15, -48.18) * mm});
            skLineSegment(sketch, "E79.15", {"start": v(-60, 40.3) * mm, "end": v(-60, -40.3) * mm});
            skArc(sketch, "E79.16", {"start": v(56.15, 48.18) * mm, "mid": v(0, 67.5) * mm, "end": v(-56.15, 48.18) * mm});
            skArc(sketch, "E79.17", {"start": v(-56.15, 48.18) * mm, "mid": v(-58.99, 44.68) * mm, "end": v(-60, 40.3) * mm});
            skArc(sketch, "E79.18", {"start": v(60, 40.3) * mm, "mid": v(58.99, 44.68) * mm, "end": v(56.15, 48.18) * mm});
            skLineSegment(sketch, "E79.19", {"start": v(60, 40.3) * mm, "end": v(60, -40.3) * mm});
            skLineSegment(sketch, "E80", {"start": v(-33, 90) * mm, "end": v(-15, 108) * mm});
            skLineSegment(sketch, "E81", {"start": v(0, 90) * mm, "end": v(0, 120) * mm, "construction": true});
            skLineSegment(sketch, "E82", {"start": v(15, 108) * mm, "end": v(15, 120) * mm});
            skLineSegment(sketch, "E83", {"start": v(-15, 108) * mm, "end": v(-15, 120) * mm});
            skArc(sketch, "E84", {"start": v(-15, 120) * mm, "mid": v(0, 135) * mm, "end": v(15, 120) * mm});
            skCircle(sketch, "E85", {"center": v(0, 120) * mm, "radius": 6 * mm});
            skLineSegment(sketch, "E86", {"start": v(15, 108) * mm, "end": v(33, 90) * mm});
            skLineSegment(sketch, "E87", {"start": v(-80, 0) * mm, "end": v(80, 0) * mm, "construction": true});
            skLineSegment(sketch, "E88.MirrorCS", {"start": v(15, -108) * mm, "end": v(33, -90) * mm});
            skLineSegment(sketch, "E89.MirrorCS", {"start": v(0, -90) * mm, "end": v(0, -120) * mm, "construction": true});
            skLineSegment(sketch, "E90.MirrorCS", {"start": v(15, -108) * mm, "end": v(15, -120) * mm});
            skArc(sketch, "E91.MirrorCS", {"start": v(-15, -120) * mm, "mid": v(0, -135) * mm, "end": v(15, -120) * mm});
            skLineSegment(sketch, "E92.MirrorCS", {"start": v(-15, -108) * mm, "end": v(-15, -120) * mm});
            skLineSegment(sketch, "E93.MirrorCS", {"start": v(-33, -90) * mm, "end": v(-15, -108) * mm});
            skCircle(sketch, "E94.MirrorC", {"center": v(0, -120) * mm, "radius": 6 * mm});
            skSolve(sketch);
        }
        {
            var Q0;
            {var subQ1=sQuery(id+"F16.wireOp",EDGE,"E79.1");Q0=makeQuery(id+"F16.imprint","IMPRINT",FACE,{"disambiguationData":[TD([[makeQuery(id+"F16.imprint","IMPRINT",EDGE,{"derivedFrom":subQ1}),1.0]])]});}
            var Q1;
            {var subQ0=sQuery(id+"F16.wireOp",EDGE,"E88.MirrorCS");Q1=makeQuery(id+"F16.imprint","IMPRINT",FACE,{"disambiguationData":[TD([[makeQuery(id+"F16.imprint","IMPRINT",EDGE,{"derivedFrom":subQ0}),1.0]])]});}
            var Q2;
            {var subQ0=sQuery(id+"F16.wireOp",EDGE,"E80");Q2=makeQuery(id+"F16.imprint","IMPRINT",FACE,{"disambiguationData":[TD([[makeQuery(id+"F16.imprint","IMPRINT",EDGE,{"derivedFrom":subQ0}),-1.0]])]});}
            var Q3;
            Q3=makeQuery(id+"F2.opExtrude","CAP_FACE",FACE,{"disambiguationData":[OSD([sQuery(id+"F0.wireOp",EDGE,"E12"),sQuery(id+"F0.wireOp",EDGE,"E13"),sQuery(id+"F0.wireOp",EDGE,"E14"),sQuery(id+"F0.wireOp",EDGE,"E15"),sQuery(id+"F0.wireOp",EDGE,"E17.filletArc"),sQuery(id+"F0.wireOp",EDGE,"E18.filletArc"),sQuery(id+"F0.wireOp",EDGE,"E19.filletArc"),sQuery(id+"F0.wireOp",EDGE,"E20.filletArc"),sQuery(id+"F0.wireOp",EDGE,"E25.0"),sQuery(id+"F0.wireOp",EDGE,"E25.1"),sQuery(id+"F0.wireOp",EDGE,"E25.2"),sQuery(id+"F0.wireOp",EDGE,"E25.3"),sQuery(id+"F0.wireOp",EDGE,"E25.4"),sQuery(id+"F0.wireOp",EDGE,"E25.5"),sQuery(id+"F0.wireOp",EDGE,"E25.6"),sQuery(id+"F0.wireOp",EDGE,"E25.7")])],"isStart":false});
            extrude(context, id + "F17", {"entities" : qUnion([Q0, Q1, Q2]), "endBound" : BoundingType.UP_TO_SURFACE, "depth" : 25 * mm, "endBoundEntityFace" : qUnion([Q3]), "offsetDistance" : 25 * mm});
        }
    });
